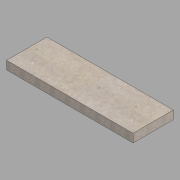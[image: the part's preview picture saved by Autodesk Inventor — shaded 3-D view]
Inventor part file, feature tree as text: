
AUTODESK INVENTOR PART (.ipt)
format: ipt  version: 2022.2 (Build 262287000, 287)  size: 110,592 bytes
history: native  units: in
note: dims shown in document units (in); Inventor stores cm internally (conversion verified against a paired STEP export)
features: extrude x1, sketch x1
ambient origin geometry x8: Origin, YZ Plane, XZ Plane, XY Plane, X Axis, Y Axis, Z Axis, Center Point
bodies: Solid1 (feature_tree)
feature tree (2):
  extrude  "Extrusion1"  Depth=19.0in
  sketch  "Sketch1"  dims[d0=59.628in d1=19.0in d2=4.0in d3=0.0in]
